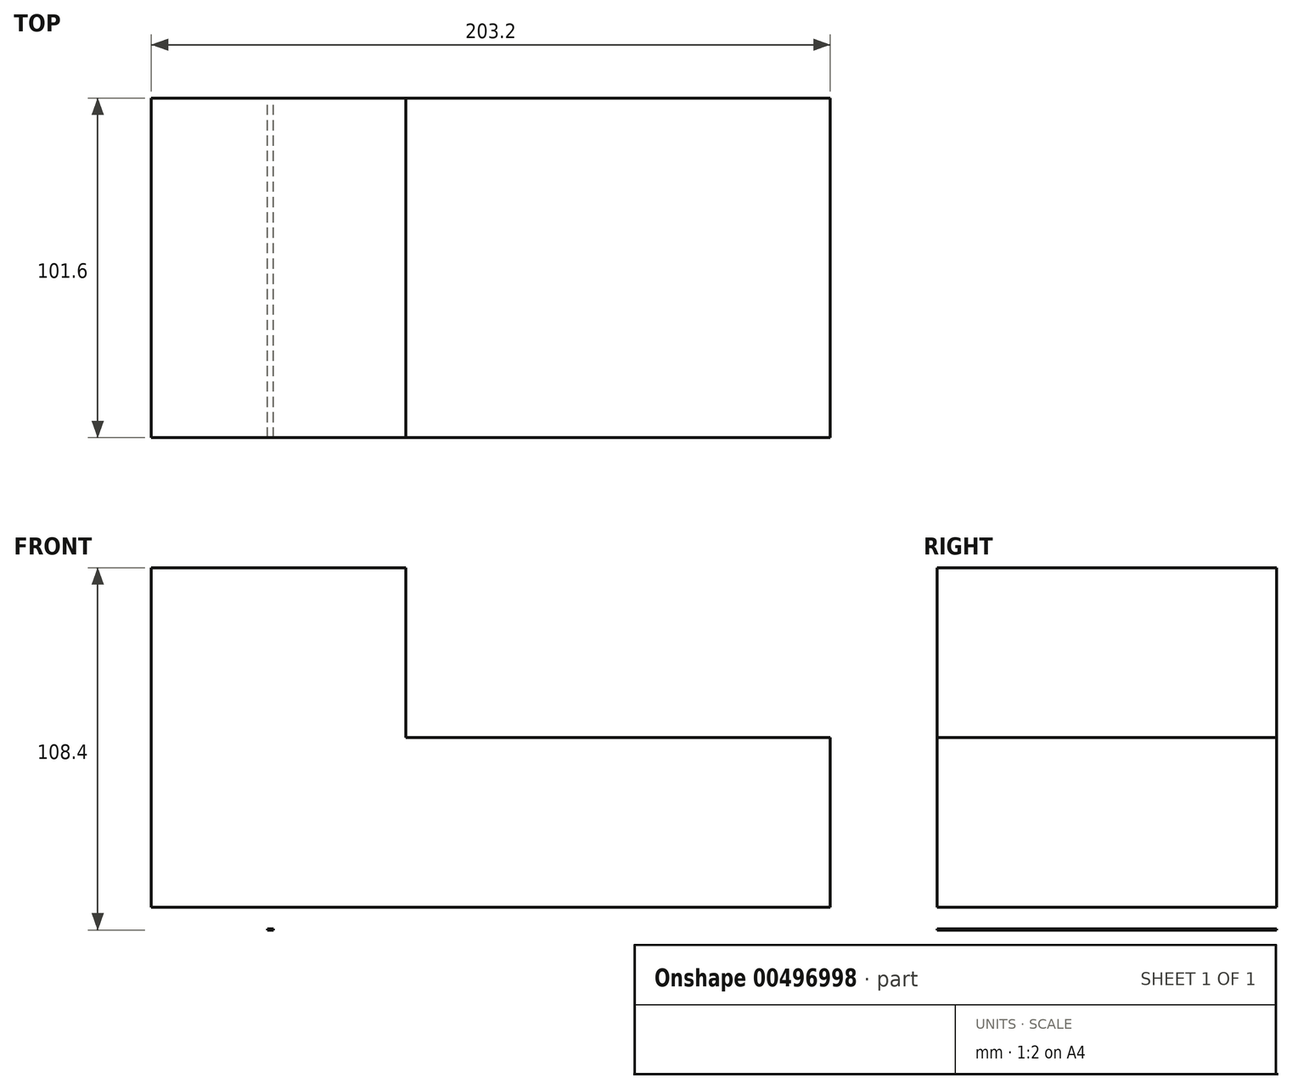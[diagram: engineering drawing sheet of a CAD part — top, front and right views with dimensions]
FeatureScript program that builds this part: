
annotation { "Feature Type Name" : "Feature", "Feature Type Description" : "" }
export const myFeature = defineFeature(function(context is Context, id is Id, definition is map)
    precondition{}
    {
        {
            var Q0;
            Q0=qCreatedBy(makeId("Front.planeOp"),FACE);
            var sketch = newSketch(context, id + "F0", { "sketchPlane" : qUnion([Q0])});
            skLineSegment(sketch, "E0.bottom", {"start": v(0, 0) * mm, "end": v(-76.2, 0) * mm});
            skLineSegment(sketch, "E0.top", {"start": v(0, 101.6) * mm, "end": v(-76.2, 101.6) * mm});
            skLineSegment(sketch, "E0.left", {"start": v(0, 0) * mm, "end": v(0, 101.6) * mm});
            skLineSegment(sketch, "E0.right", {"start": v(-76.2, 0) * mm, "end": v(-76.2, 101.6) * mm});
            skLineSegment(sketch, "E1.bottom", {"start": v(-39.61, -6.5) * mm, "end": v(-41.43, -6.5) * mm});
            skLineSegment(sketch, "E1.top", {"start": v(-39.61, -6.8) * mm, "end": v(-41.43, -6.8) * mm});
            skLineSegment(sketch, "E1.left", {"start": v(-39.61, -6.5) * mm, "end": v(-39.61, -6.8) * mm});
            skLineSegment(sketch, "E1.right", {"start": v(-41.43, -6.5) * mm, "end": v(-41.43, -6.8) * mm});
            skLineSegment(sketch, "E2.bottom", {"start": v(0, 0) * mm, "end": v(127, 0) * mm});
            skLineSegment(sketch, "E2.top", {"start": v(0, 50.8) * mm, "end": v(127, 50.8) * mm});
            skLineSegment(sketch, "E2.left", {"start": v(0, 0) * mm, "end": v(0, 50.8) * mm});
            skLineSegment(sketch, "E2.right", {"start": v(127, 0) * mm, "end": v(127, 50.8) * mm});
            skSolve(sketch);
        }
        {
            var Q0;
            Q0 = qSketchRegion(id + "F0", true);
            extrude(context, id + "F1", {"entities" : qUnion([Q0]), "depth" : 101.6 * mm});
        }
    });
